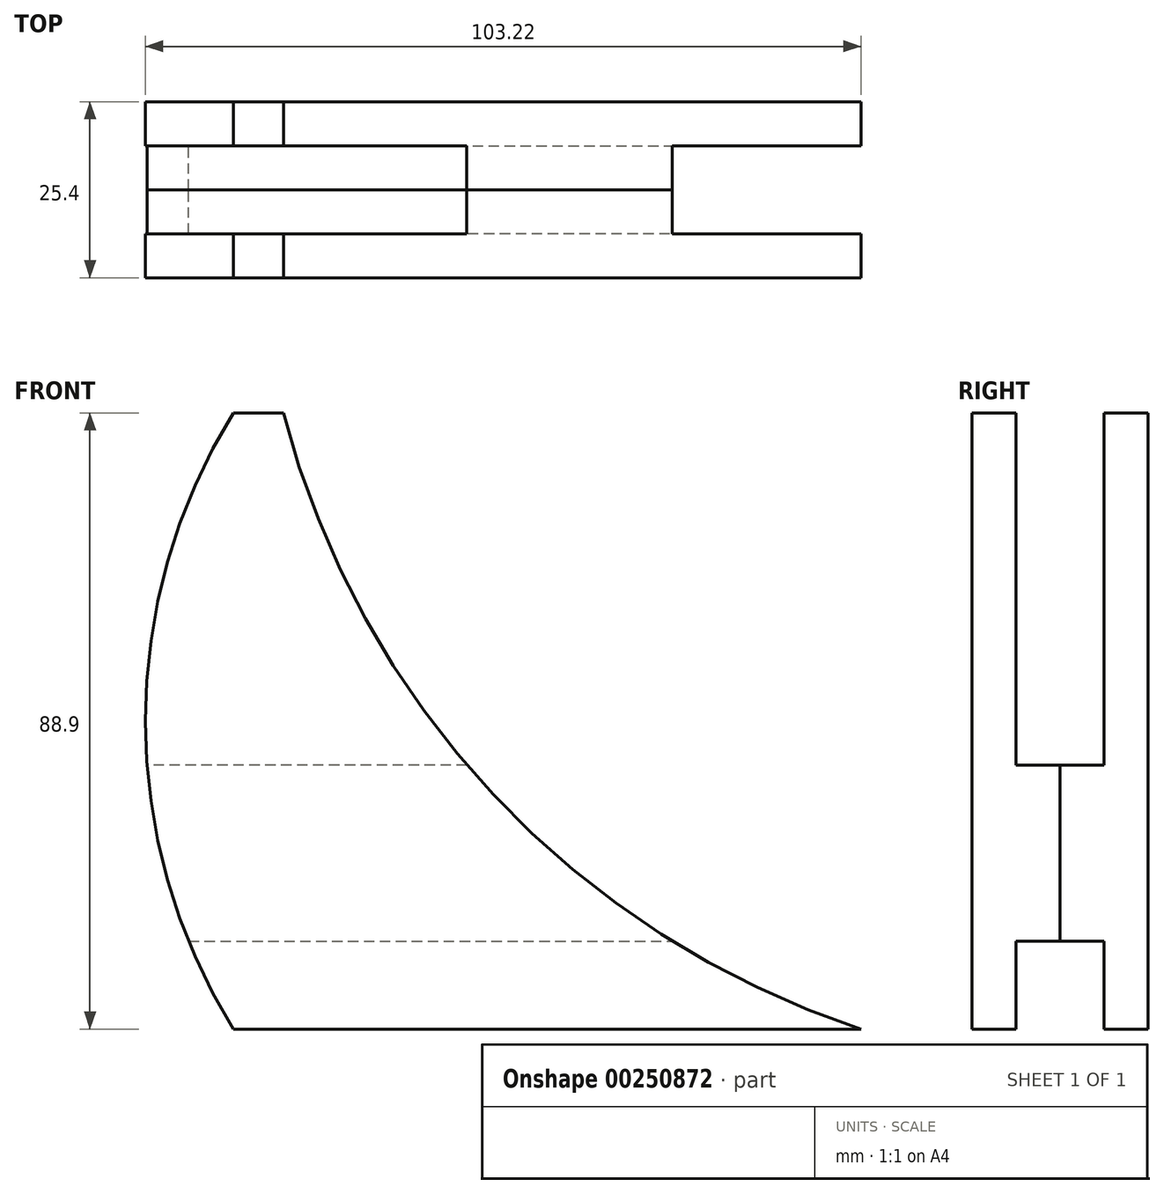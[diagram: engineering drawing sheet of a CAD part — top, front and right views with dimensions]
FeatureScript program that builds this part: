
annotation { "Feature Type Name" : "Feature", "Feature Type Description" : "" }
export const myFeature = defineFeature(function(context is Context, id is Id, definition is map)
    precondition{}
    {
        {
            var Q0;
            Q0=qCreatedBy(makeId("Front.planeOp"),FACE);
            var sketch = newSketch(context, id + "F0", { "sketchPlane" : qUnion([Q0])});
            skLineSegment(sketch, "E0.bottom", {"start": v(0, 0) * mm, "end": v(104.78, 0) * mm});
            skLineSegment(sketch, "E0.top", {"start": v(0, -88.9) * mm, "end": v(104.78, -88.9) * mm});
            skLineSegment(sketch, "E0.left", {"start": v(0, 0) * mm, "end": v(0, -88.9) * mm});
            skLineSegment(sketch, "E0.right", {"start": v(104.78, 0) * mm, "end": v(104.78, -88.9) * mm});
            skLineSegment(sketch, "E1", {"start": v(142.87, 0) * mm, "end": v(142.87, 31.75) * mm});
            skLineSegment(sketch, "E2", {"start": v(104.78, 0) * mm, "end": v(142.87, 0) * mm});
            skCircle(sketch, "E3", {"center": v(142.87, 31.75) * mm, "radius": 127 * mm});
            skLineSegment(sketch, "E4", {"start": v(104.78, 0) * mm, "end": v(84.14, 0) * mm});
            skLineSegment(sketch, "E5", {"start": v(84.14, 0) * mm, "end": v(84.14, -44.45) * mm});
            skCircle(sketch, "E6", {"center": v(84.14, -44.45) * mm, "radius": 84.14 * mm});
            skSolve(sketch);
        }
        {
            var Q0;
            {var subQ1=sQuery(id+"F0.wireOp",EDGE,"E0.bottom");var subQ5=sQuery(id+"F0.wireOp",EDGE,"E6");var subQ7=makeQuery(id+"F0.imprint","INTERSECT",VERTEX,{"derivedFrom":[subQ1,subQ5]});Q0=makeQuery(id+"F0.imprint","IMPRINT",FACE,{"disambiguationData":[TD([[makeQuery(id+"F0.imprint","IMPRINT",EDGE,{"disambiguationData":[TD([[subQ7,-1.0]])],"derivedFrom":subQ1}),-1.0]])]});}
            extrude(context, id + "F1", {"entities" : qUnion([Q0]), "depth" : 6.35 * mm});
        }
        {
            var Q0;
            Q0=makeQuery(id+"F1.opExtrude","CAP_FACE",FACE,{"disambiguationData":[OSD([sQuery(id+"F0.wireOp",EDGE,"E0.bottom"),sQuery(id+"F0.wireOp",EDGE,"E0.top"),sQuery(id+"F0.wireOp",EDGE,"E3"),sQuery(id+"F0.wireOp",EDGE,"E6")])],"isStart":false});
            var sketch = newSketch(context, id + "F2", { "sketchPlane" : qUnion([Q0])});
            skLineSegment(sketch, "E7", {"start": v(6.22, -76.2) * mm, "end": v(75.97, -76.2) * mm});
            skLineSegment(sketch, "E8", {"start": v(46.36, -50.8) * mm, "end": v(0.24, -50.8) * mm});
            skArc(sketch, "E9.0", {"start": v(12.7, 0) * mm, "mid": v(0, -44.45) * mm, "end": v(12.7, -88.9) * mm});
            skArc(sketch, "E10.0", {"start": v(19.9, 0) * mm, "mid": v(50.2, -55.1) * mm, "end": v(103.22, -88.9) * mm});
            skSolve(sketch);
        }
        {
            var Q0;
            Q0=qSketchRegion(id+"F2",true);
            extrude(context, id + "F3", {"entities" : qUnion([Q0]), "operationType" : NewBodyOperationType.ADD, "depth" : 6.35 * mm});
        }
        {
            var Q0;
            Q0=makeQuery(id+"F3.opExtrude","CAP_FACE",FACE,{"disambiguationData":[OSD([sQuery(id+"F2.wireOp",EDGE,"E7"),sQuery(id+"F2.wireOp",EDGE,"E8"),sQuery(id+"F2.wireOp",EDGE,"E9.0"),sQuery(id+"F2.wireOp",EDGE,"E10.0")])],"isStart":false});
            extrude(context, id + "F4", {"entities" : qUnion([Q0]), "depth" : 6.35 * mm});
        }
        {
            var Q0;
            Q0=makeQuery(id+"F4.opExtrude","CAP_FACE",FACE,{"disambiguationData":[OSD([sQuery(id+"F2.wireOp",EDGE,"E7"),sQuery(id+"F2.wireOp",EDGE,"E8"),sQuery(id+"F2.wireOp",EDGE,"E9.0"),sQuery(id+"F2.wireOp",EDGE,"E10.0")])],"isStart":false});
            var sketch = newSketch(context, id + "F5", { "sketchPlane" : qUnion([Q0])});
            skLineSegment(sketch, "E11.0.0", {"start": v(12.7, 0) * mm, "end": v(19.9, 0) * mm});
            skArc(sketch, "E11.0.1", {"start": v(19.9, 0) * mm, "mid": v(50.2, -55.1) * mm, "end": v(103.22, -88.9) * mm});
            skLineSegment(sketch, "E11.0.2", {"start": v(103.22, -88.9) * mm, "end": v(12.7, -88.9) * mm});
            skArc(sketch, "E11.0.3", {"start": v(12.7, -88.9) * mm, "mid": v(0, -44.45) * mm, "end": v(12.7, 0) * mm});
            skSolve(sketch);
        }
        {
            var Q0;
            Q0=qSketchRegion(id+"F5",true);
            extrude(context, id + "F6", {"entities" : qUnion([Q0]), "operationType" : NewBodyOperationType.ADD, "depth" : 6.35 * mm});
        }
    });
